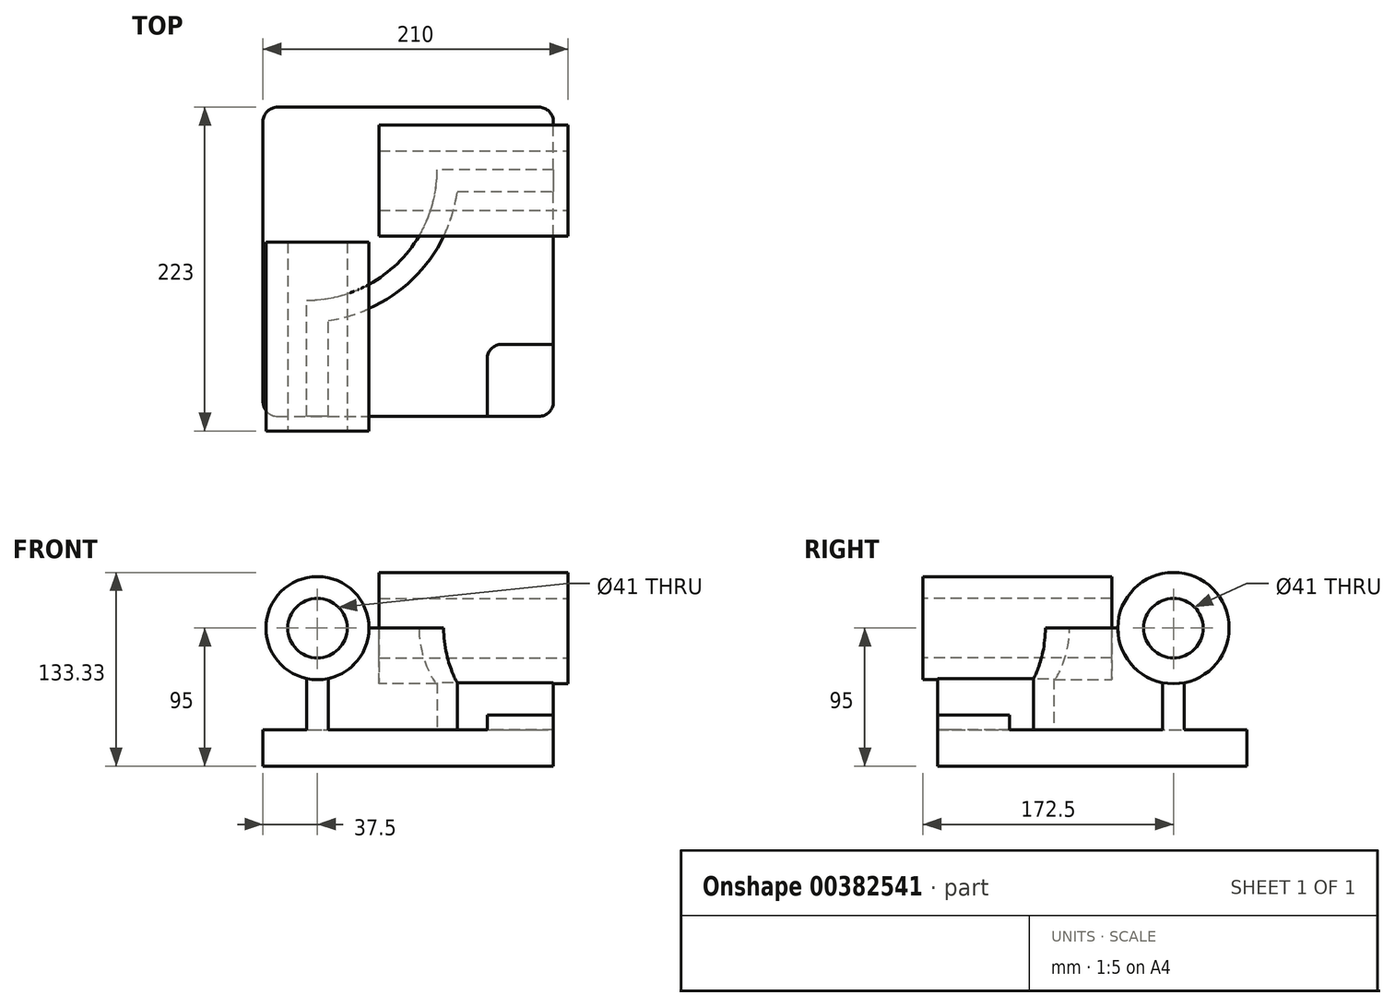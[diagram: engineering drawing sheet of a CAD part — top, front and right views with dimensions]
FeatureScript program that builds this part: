
annotation { "Feature Type Name" : "Feature", "Feature Type Description" : "" }
export const myFeature = defineFeature(function(context is Context, id is Id, definition is map)
    precondition{}
    {
        {
            assignVariable(context, id + "F0", {"name" : "D", "anyValue" : 130 * mm});
        }
        {
            var Q0;
            Q0=qCreatedBy(makeId("Top.planeOp"),FACE);
            var sketch = newSketch(context, id + "F1", { "sketchPlane" : qUnion([Q0])});
            skLineSegment(sketch, "E0.bottom", {"start": v(10, 0) * mm, "end": v(190, 0) * mm});
            skLineSegment(sketch, "E0.top", {"start": v(10, 213) * mm, "end": v(190, 213) * mm});
            skLineSegment(sketch, "E0.left", {"start": v(0, 10) * mm, "end": v(0, 203) * mm});
            skLineSegment(sketch, "E0.right", {"start": v(200, 10) * mm, "end": v(200, 203) * mm});
            skPoint(sketch, "E1.visualSharp", {"position": v(200, 0) * mm});
            skArc(sketch, "E1.filletArc", {"start": v(190, 0) * mm, "mid": v(197.07, 2.93) * mm, "end": v(200, 10) * mm});
            skPoint(sketch, "E2.visualSharp", {"position": v(200, 213) * mm});
            skArc(sketch, "E2.filletArc", {"start": v(200, 203) * mm, "mid": v(197.07, 210.07) * mm, "end": v(190, 213) * mm});
            skPoint(sketch, "E3.visualSharp", {"position": v(0, 213) * mm});
            skArc(sketch, "E3.filletArc", {"start": v(10, 213) * mm, "mid": v(2.93, 210.07) * mm, "end": v(0, 203) * mm});
            skPoint(sketch, "E4.visualSharp", {"position": v(0, 0) * mm});
            skArc(sketch, "E4.filletArc", {"start": v(0, 10) * mm, "mid": v(2.93, 2.93) * mm, "end": v(10, 0) * mm});
            skSolve(sketch);
        }
        {
            var Q0;
            Q0 = qSketchRegion(id + "F1", true);
            extrude(context, id + "F2", {"entities" : qUnion([Q0]), "depth" : 25 * mm});
        }
        {
            var Q0;
            Q0=makeQuery(id+"F2.opExtrude","CAP_FACE",FACE,{"disambiguationData":[OSD([sQuery(id+"F1.wireOp",EDGE,"E0.bottom"),sQuery(id+"F1.wireOp",EDGE,"E0.top"),sQuery(id+"F1.wireOp",EDGE,"E0.left"),sQuery(id+"F1.wireOp",EDGE,"E0.right"),sQuery(id+"F1.wireOp",EDGE,"E1.filletArc"),sQuery(id+"F1.wireOp",EDGE,"E2.filletArc"),sQuery(id+"F1.wireOp",EDGE,"E3.filletArc"),sQuery(id+"F1.wireOp",EDGE,"E4.filletArc")])],"isStart":false});
            var sketch = newSketch(context, id + "F3", { "sketchPlane" : qUnion([Q0])});
            skLineSegment(sketch, "E5", {"start": v(30, 0) * mm, "end": v(30, 80) * mm});
            skLineSegment(sketch, "E6", {"start": v(120, 170) * mm, "end": v(200, 170) * mm});
            skLineSegment(sketch, "E7", {"start": v(200, 170) * mm, "end": v(120, 170) * mm, "construction": true});
            skLineSegment(sketch, "E8", {"start": v(30, 0) * mm, "end": v(30, 80) * mm, "construction": true});
            skPoint(sketch, "E8.endSnap0", {"position": v(30, 40) * mm});
            skArc(sketch, "E9", {"start": v(30, 80) * mm, "mid": v(93.64, 106.36) * mm, "end": v(120, 170) * mm});
            skPoint(sketch, "E10.orphan", {"position": v(30, 304.27) * mm});
            skLineSegment(sketch, "E11", {"start": v(120, 170) * mm, "end": v(-67.14, 170) * mm, "construction": true});
            skPoint(sketch, "E12.end.orphan", {"position": v(0, 277.7) * mm});
            skLineSegment(sketch, "E13", {"start": v(30, 80) * mm, "end": v(30, 304.27) * mm, "construction": true});
            skLineSegment(sketch, "E14.0", {"start": v(133.92, 155) * mm, "end": v(200, 155) * mm});
            skArc(sketch, "E14.1", {"start": v(45, 66.08) * mm, "mid": v(104.25, 95.75) * mm, "end": v(133.92, 155) * mm});
            skLineSegment(sketch, "E14.2", {"start": v(45, 0) * mm, "end": v(45, 66.08) * mm});
            skLineSegment(sketch, "E15", {"start": v(45, 0) * mm, "end": v(30, 0) * mm});
            skLineSegment(sketch, "E16", {"start": v(200, 155) * mm, "end": v(200, 170) * mm});
            skSolve(sketch);
        }
        {
            var Q0;
            Q0 = qSketchRegion(id + "F3", true);
            extrude(context, id + "F4", {"entities" : qUnion([Q0]), "operationType" : NewBodyOperationType.ADD, "depth" : 70 * mm});
        }
        {
            var Q0;
            Q0=makeQuery(id+"F4.boolean.opBoolean","MERGE",FACE,{"derivedFrom":[makeQuery(id+"F2.opExtrude","SWEPT_FACE",FACE,{"disambiguationData":[OSD([sQuery(id+"F1.wireOp",EDGE,"E0.bottom")])]}),makeQuery(id+"F4.opExtrude","SWEPT_FACE",FACE,{"disambiguationData":[OSD([sQuery(id+"F3.wireOp",EDGE,"E15")])]})]});
            var sketch = newSketch(context, id + "F5", { "sketchPlane" : qUnion([Q0])});
            skPoint(sketch, "E17", {"position": v(37.5, 95) * mm});
            skCircle(sketch, "E18", {"center": v(37.5, 95) * mm, "radius": 35.5 * mm});
            skSolve(sketch);
        }
        {
            var Q0;
            Q0 = qSketchRegion(id + "F5", true);
            extrude(context, id + "F6", {"entities" : qUnion([Q0]), "operationType" : NewBodyOperationType.ADD, "depth" : 10 * mm, "hasSecondDirection" : true, "secondDirectionOppositeDirection" : true, "secondDirectionDepth" : getVariable(context, 'D') - 10 * mm});
        }
        {
            var Q0;
            Q0=makeQuery(id+"F4.boolean.opBoolean","MERGE",FACE,{"derivedFrom":[makeQuery(id+"F2.opExtrude","SWEPT_FACE",FACE,{"disambiguationData":[OSD([sQuery(id+"F1.wireOp",EDGE,"E0.right")])]}),makeQuery(id+"F4.opExtrude","SWEPT_FACE",FACE,{"disambiguationData":[OSD([sQuery(id+"F3.wireOp",EDGE,"E16")])]})]});
            var sketch = newSketch(context, id + "F7", { "sketchPlane" : qUnion([Q0])});
            skPoint(sketch, "E19", {"position": v(162.5, 95) * mm});
            skCircle(sketch, "E20", {"center": v(162.5, 95) * mm, "radius": 38.33 * mm});
            skSolve(sketch);
        }
        {
            var Q0;
            Q0 = qSketchRegion(id + "F7", true);
            extrude(context, id + "F8", {"entities" : qUnion([Q0]), "operationType" : NewBodyOperationType.ADD, "depth" : 10 * mm, "hasSecondDirection" : true, "secondDirectionOppositeDirection" : true, "secondDirectionDepth" : getVariable(context, 'D') - 10 * mm});
        }
        {
            var Q0;
            Q0=makeQuery(id+"F6.opExtrude","CAP_FACE",FACE,{"disambiguationData":[OSD([sQuery(id+"F5.wireOp",EDGE,"E18")])],"isStart":false});
            var sketch = newSketch(context, id + "F9", { "sketchPlane" : qUnion([Q0])});
            skCircle(sketch, "E21", {"center": v(37.5, 95) * mm, "radius": 20.5 * mm});
            skSolve(sketch);
        }
        {
            var Q0;
            Q0 = qSketchRegion(id + "F9", true);
            extrude(context, id + "F10", {"entities" : qUnion([Q0]), "operationType" : NewBodyOperationType.REMOVE, "endBound" : BoundingType.THROUGH_ALL, "oppositeDirection" : true, "depth" : 25 * mm});
        }
        {
            var Q0;
            Q0=makeQuery(id+"F8.opExtrude","CAP_FACE",FACE,{"disambiguationData":[OSD([sQuery(id+"F7.wireOp",EDGE,"E20")])],"isStart":false});
            var sketch = newSketch(context, id + "F11", { "sketchPlane" : qUnion([Q0])});
            skCircle(sketch, "E22", {"center": v(162.5, 95) * mm, "radius": 20.5 * mm});
            skSolve(sketch);
        }
        {
            var Q0;
            Q0 = qSketchRegion(id + "F11", true);
            extrude(context, id + "F12", {"entities" : qUnion([Q0]), "operationType" : NewBodyOperationType.REMOVE, "endBound" : BoundingType.THROUGH_ALL, "oppositeDirection" : true, "depth" : 25 * mm});
        }
        {
            var Q0;
            {var subQ0=sQuery(id+"F1.wireOp",EDGE,"E1.filletArc");var subQ1=sQuery(id+"F1.wireOp",EDGE,"E0.right");var subQ2=sQuery(id+"F1.wireOp",EDGE,"E0.bottom");Q0=makeQuery(id+"F4.boolean.opBoolean","SPLIT",FACE,{"disambiguationData":[TD([makeQuery(id+"F2.opExtrude","SWEPT_FACE",FACE,{"disambiguationData":[OSD([subQ0])]})])],"derivedFrom":makeQuery(id+"F2.opExtrude","CAP_FACE",FACE,{"disambiguationData":[OSD([subQ2,sQuery(id+"F1.wireOp",EDGE,"E0.top"),sQuery(id+"F1.wireOp",EDGE,"E0.left"),subQ1,subQ0,sQuery(id+"F1.wireOp",EDGE,"E2.filletArc"),sQuery(id+"F1.wireOp",EDGE,"E3.filletArc"),sQuery(id+"F1.wireOp",EDGE,"E4.filletArc")])],"isStart":false})});}
            var sketch = newSketch(context, id + "F13", { "sketchPlane" : qUnion([Q0])});
            skLineSegment(sketch, "E23", {"start": v(200, 49.62) * mm, "end": v(164.42, 49.62) * mm});
            skLineSegment(sketch, "E24", {"start": v(154.42, 39.62) * mm, "end": v(154.42, 0) * mm});
            skLineSegment(sketch, "E25.0", {"start": v(200, 10) * mm, "end": v(200, 49.62) * mm});
            skArc(sketch, "E26.0", {"start": v(190, 0) * mm, "mid": v(197.07, 2.93) * mm, "end": v(200, 10) * mm});
            skLineSegment(sketch, "E27.0", {"start": v(45, 0) * mm, "end": v(190, 0) * mm});
            skPoint(sketch, "E28.orphan", {"position": v(200, 155) * mm});
            skPoint(sketch, "E29.visualSharp", {"position": v(154.42, 49.62) * mm});
            skArc(sketch, "E29.filletArc", {"start": v(164.42, 49.62) * mm, "mid": v(157.35, 46.69) * mm, "end": v(154.42, 39.62) * mm});
            skSolve(sketch);
        }
        {
            var Q0;
            Q0 = qSketchRegion(id + "F13", true);
            extrude(context, id + "F14", {"entities" : qUnion([Q0]), "operationType" : NewBodyOperationType.ADD, "depth" : 10 * mm});
        }
    });
